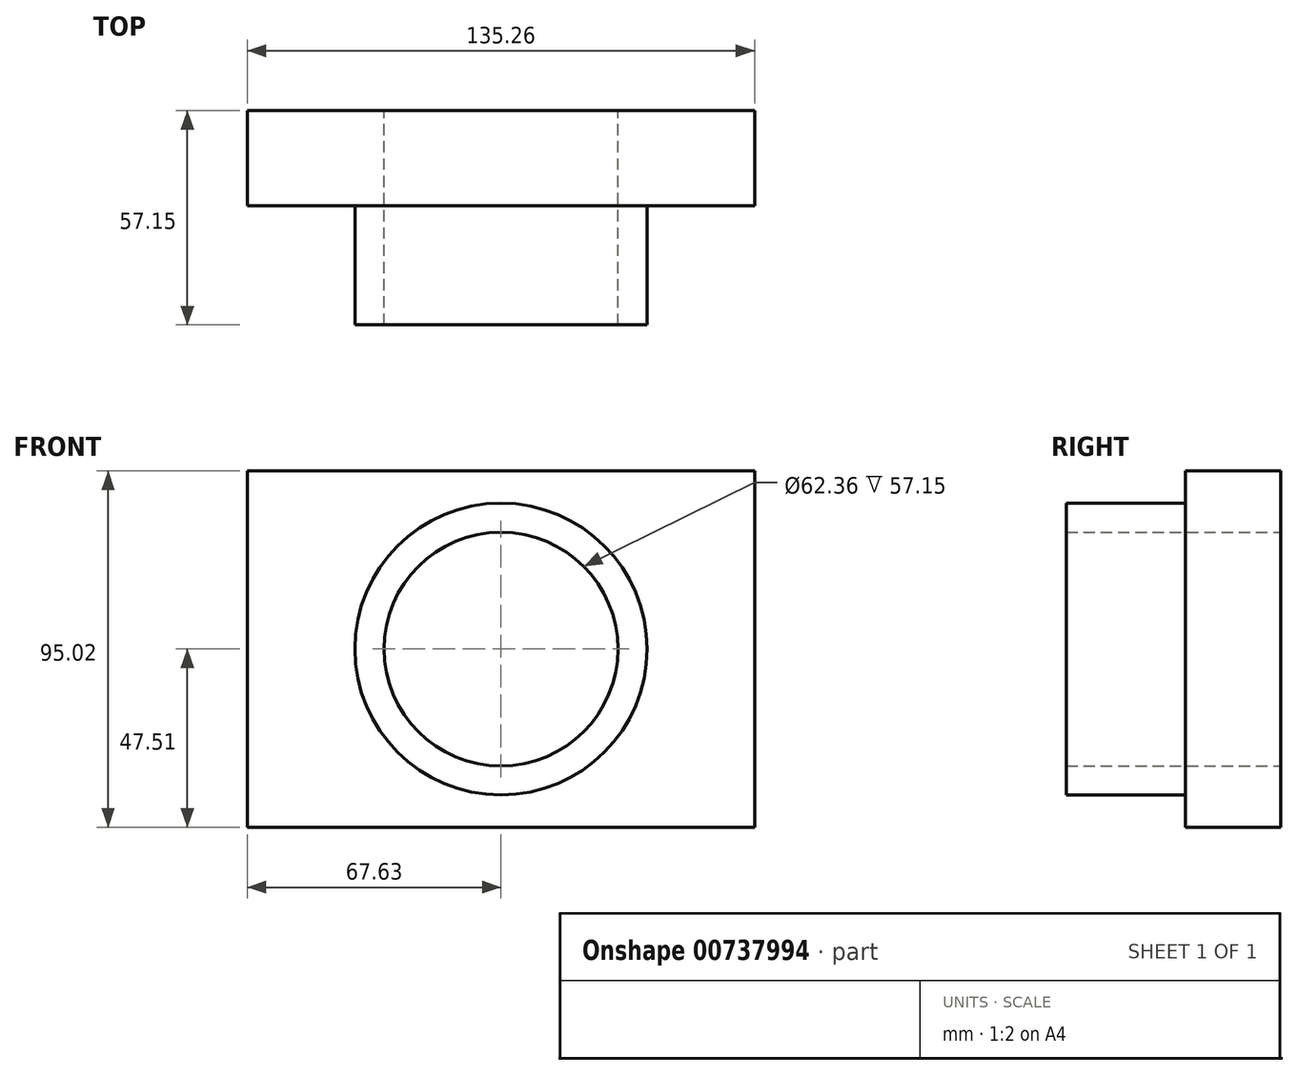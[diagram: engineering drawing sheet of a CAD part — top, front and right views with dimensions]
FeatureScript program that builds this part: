
annotation { "Feature Type Name" : "Feature", "Feature Type Description" : "" }
export const myFeature = defineFeature(function(context is Context, id is Id, definition is map)
    precondition{}
    {
        {
            var Q0;
            Q0=qCreatedBy(makeId("Front.planeOp"),FACE);
            var sketch = newSketch(context, id + "F0", { "sketchPlane" : qUnion([Q0])});
            skLineSegment(sketch, "E0.bottom", {"start": v(67.63, 47.5) * mm, "end": v(-67.63, 47.5) * mm});
            skLineSegment(sketch, "E0.top", {"start": v(67.63, -47.5) * mm, "end": v(-67.63, -47.5) * mm});
            skLineSegment(sketch, "E0.left", {"start": v(67.63, 47.5) * mm, "end": v(67.63, -47.5) * mm});
            skLineSegment(sketch, "E0.right", {"start": v(-67.63, 47.5) * mm, "end": v(-67.63, -47.5) * mm});
            skPoint(sketch, "E0.middle", {"position": v(0, 0) * mm});
            skSolve(sketch);
        }
        {
            var Q0;
            Q0 = qSketchRegion(id + "F0", true);
            extrude(context, id + "F1", {"entities" : qUnion([Q0]), "depth" : 25.4 * mm, "offsetDistance" : 25.4 * mm});
        }
        {
            var Q0;
            Q0=makeQuery(id+"F1.opExtrude","CAP_FACE",FACE,{"disambiguationData":[OSD([sQuery(id+"F0.wireOp",EDGE,"E0.bottom"),sQuery(id+"F0.wireOp",EDGE,"E0.top"),sQuery(id+"F0.wireOp",EDGE,"E0.left"),sQuery(id+"F0.wireOp",EDGE,"E0.right")])],"isStart":false});
            var sketch = newSketch(context, id + "F2", { "sketchPlane" : qUnion([Q0])});
            skCircle(sketch, "E1", {"center": v(0, 0) * mm, "radius": 38.94 * mm});
            skSolve(sketch);
        }
        {
            var Q0;
            Q0 = qSketchRegion(id + "F2", true);
            extrude(context, id + "F3", {"entities" : qUnion([Q0]), "operationType" : NewBodyOperationType.ADD, "depth" : 31.75 * mm, "offsetDistance" : 25.4 * mm});
        }
        {
            var Q0;
            Q0=qCreatedBy(makeId("Front.planeOp"),FACE);
            var sketch = newSketch(context, id + "F4", { "sketchPlane" : qUnion([Q0])});
            skCircle(sketch, "E2", {"center": v(0, 0) * mm, "radius": 31.18 * mm});
            skSolve(sketch);
        }
        {
            var Q0;
            Q0 = qSketchRegion(id + "F4", true);
            extrude(context, id + "F5", {"entities" : qUnion([Q0]), "operationType" : NewBodyOperationType.REMOVE, "depth" : 76.2 * mm, "offsetDistance" : 25.4 * mm});
        }
    });
